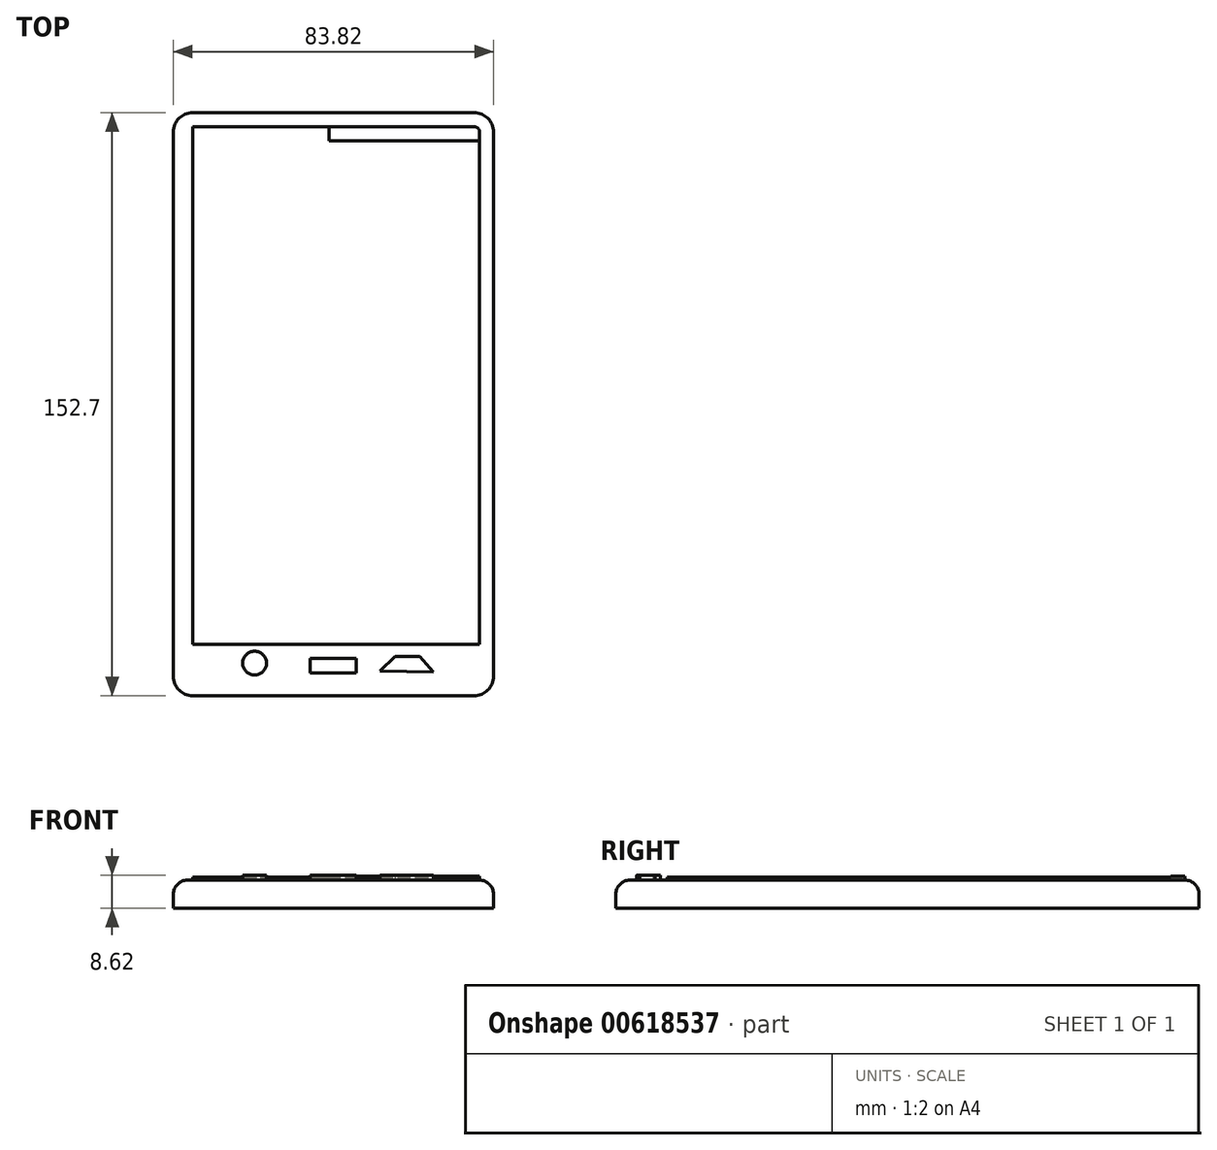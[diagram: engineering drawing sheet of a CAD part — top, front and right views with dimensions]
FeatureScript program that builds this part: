
annotation { "Feature Type Name" : "Feature", "Feature Type Description" : "" }
export const myFeature = defineFeature(function(context is Context, id is Id, definition is map)
    precondition{}
    {
        {
            var Q0;
            Q0=qCreatedBy(makeId("Top.planeOp"),FACE);
            var sketch = newSketch(context, id + "F0", { "sketchPlane" : qUnion([Q0])});
            skLineSegment(sketch, "E0.bottom", {"start": v(-77.85, 109.1) * mm, "end": v(5.97, 109.1) * mm});
            skLineSegment(sketch, "E0.top", {"start": v(-77.85, -43.6) * mm, "end": v(5.97, -43.6) * mm});
            skLineSegment(sketch, "E0.left", {"start": v(-77.85, 109.1) * mm, "end": v(-77.85, -43.6) * mm});
            skLineSegment(sketch, "E0.right", {"start": v(5.97, 109.1) * mm, "end": v(5.97, -43.6) * mm});
            skSolve(sketch);
        }
        {
            var Q0;
            Q0=makeQuery(id+"F0.imprint","IMPRINT",FACE,{"disambiguationData":[TD([[makeQuery(id+"F0.imprint","IMPRINT",EDGE,{"derivedFrom":sQuery(id+"F0.wireOp",EDGE,"E0.bottom")}),-1.0]])]});
            extrude(context, id + "F1", {"entities" : qUnion([Q0]), "depth" : 7.35 * mm, "offsetDistance" : 25.4 * mm});
        }
        {
            var Q0;
            Q0=makeQuery(id+"F1.opExtrude","SWEPT_EDGE",EDGE,{"disambiguationData":[OSD([sQuery(id+"F0.wireOp",EDGE,"E0.top"),sQuery(id+"F0.wireOp",EDGE,"E0.right")])]});
            var Q1;
            Q1=makeQuery(id+"F1.opExtrude","SWEPT_EDGE",EDGE,{"disambiguationData":[OSD([sQuery(id+"F0.wireOp",EDGE,"E0.top"),sQuery(id+"F0.wireOp",EDGE,"E0.left")])]});
            var Q2;
            Q2=makeQuery(id+"F1.opExtrude","SWEPT_EDGE",EDGE,{"disambiguationData":[OSD([sQuery(id+"F0.wireOp",EDGE,"E0.bottom"),sQuery(id+"F0.wireOp",EDGE,"E0.left")])]});
            var Q3;
            Q3=makeQuery(id+"F1.opExtrude","SWEPT_EDGE",EDGE,{"disambiguationData":[OSD([sQuery(id+"F0.wireOp",EDGE,"E0.bottom"),sQuery(id+"F0.wireOp",EDGE,"E0.right")])]});
            fillet(context, id + "F2", {"entities" : qUnion([Q0, Q1, Q2, Q3]), "radius" : 5.08 * mm, "tangentPropagation" : true, "allowEdgeOverflow" : false});
        }
        {
            var Q0;
            Q0=makeQuery(id+"F1.opExtrude","CAP_EDGE",EDGE,{"disambiguationData":[OSD([sQuery(id+"F0.wireOp",EDGE,"E0.right")])],"isStart":false});
            var Q1;
            Q1=makeQuery(id+"F1.opExtrude","CAP_EDGE",EDGE,{"disambiguationData":[OSD([sQuery(id+"F0.wireOp",EDGE,"E0.left")])],"isStart":false});
            fillet(context, id + "F3", {"entities" : qUnion([Q0, Q1]), "radius" : 3.68 * mm, "tangentPropagation" : true, "allowEdgeOverflow" : false});
        }
        {
            var Q0;
            Q0=makeQuery(id+"F1.opExtrude","CAP_FACE",FACE,{"disambiguationData":[OSD([sQuery(id+"F0.wireOp",EDGE,"E0.bottom"),sQuery(id+"F0.wireOp",EDGE,"E0.top"),sQuery(id+"F0.wireOp",EDGE,"E0.left"),sQuery(id+"F0.wireOp",EDGE,"E0.right")])],"isStart":false});
            var sketch = newSketch(context, id + "F4", { "sketchPlane" : qUnion([Q0])});
            skLineSegment(sketch, "E1.bottom", {"start": v(-72.77, 105.41) * mm, "end": v(2.29, 105.41) * mm});
            skLineSegment(sketch, "E1.top", {"start": v(-72.77, -30.16) * mm, "end": v(2.29, -30.16) * mm});
            skLineSegment(sketch, "E1.left", {"start": v(-72.77, 105.41) * mm, "end": v(-72.77, -30.16) * mm});
            skLineSegment(sketch, "E1.right", {"start": v(2.29, 105.41) * mm, "end": v(2.29, -30.16) * mm});
            skLineSegment(sketch, "E2.bottom", {"start": v(-42.1, -33.78) * mm, "end": v(-30.03, -33.78) * mm});
            skLineSegment(sketch, "E2.top", {"start": v(-42.1, -37.65) * mm, "end": v(-30.03, -37.65) * mm});
            skLineSegment(sketch, "E2.left", {"start": v(-42.1, -33.78) * mm, "end": v(-42.1, -37.65) * mm});
            skLineSegment(sketch, "E2.right", {"start": v(-30.03, -33.78) * mm, "end": v(-30.03, -37.65) * mm});
            skLineSegment(sketch, "E3", {"start": v(-56.59, -30.16) * mm, "end": v(-56.59, -39.93) * mm});
            skLineSegment(sketch, "E4", {"start": v(-56.59, -39.93) * mm, "end": v(-56.59, -35.04) * mm});
            skLineSegment(sketch, "E5", {"start": v(-56.59, -35.04) * mm, "end": v(-85.32, -35.04) * mm});
            skCircle(sketch, "E6", {"center": v(-56.59, -35.04) * mm, "radius": 3.12 * mm});
            skLineSegment(sketch, "E7", {"start": v(-23.75, -37.16) * mm, "end": v(-19.88, -33.3) * mm});
            skLineSegment(sketch, "E8", {"start": v(-19.88, -33.3) * mm, "end": v(-13.36, -33.3) * mm});
            skLineSegment(sketch, "E9", {"start": v(-13.36, -33.3) * mm, "end": v(-9.75, -37.4) * mm});
            skLineSegment(sketch, "E10", {"start": v(-23.75, -37.16) * mm, "end": v(-9.75, -37.4) * mm});
            skSolve(sketch);
        }
        {
            var Q0;
            {var subQ7=sQuery(id+"F4.wireOp",EDGE,"E1.top");Q0=makeQuery(id+"F4.imprint","IMPRINT",FACE,{"disambiguationData":[TD([[makeQuery(id+"F4.imprint","IMPRINT",EDGE,{"derivedFrom":subQ7}),1.0]])]});}
            extrude(context, id + "F5", {"entities" : qUnion([Q0]), "operationType" : NewBodyOperationType.ADD, "depth" : 0.76 * mm, "offsetDistance" : 25.4 * mm});
        }
        {
            var Q0;
            Q0=makeQuery(id+"F4.imprint","IMPRINT",FACE,{"disambiguationData":[TD([[makeQuery(id+"F4.imprint","IMPRINT",EDGE,{"derivedFrom":sQuery(id+"F4.wireOp",EDGE,"E2.bottom")}),-1.0]])]});
            var Q1;
            {var subQ1=sQuery(id+"F4.wireOp",EDGE,"E3");var subQ3=sQuery(id+"F4.wireOp",EDGE,"E6");var subQ4=makeQuery(id+"F4.imprint","INTERSECT",VERTEX,{"derivedFrom":[subQ1,subQ3]});Q1=makeQuery(id+"F4.imprint","IMPRINT",FACE,{"disambiguationData":[TD([[makeQuery(id+"F4.imprint","IMPRINT",EDGE,{"disambiguationData":[TD([[subQ4,1.0]])],"derivedFrom":subQ3}),1.0]])]});}
            var Q2;
            {var subQ1=sQuery(id+"F4.wireOp",EDGE,"E3");var subQ3=sQuery(id+"F4.wireOp",EDGE,"E6");var subQ4=makeQuery(id+"F4.imprint","INTERSECT",VERTEX,{"derivedFrom":[subQ1,subQ3]});Q2=makeQuery(id+"F4.imprint","IMPRINT",FACE,{"disambiguationData":[TD([[makeQuery(id+"F4.imprint","IMPRINT",EDGE,{"disambiguationData":[TD([[subQ4,-1.0]])],"derivedFrom":subQ3}),1.0]])]});}
            var Q3;
            {var subQ1=sQuery(id+"F4.wireOp",EDGE,"E4");var subQ3=sQuery(id+"F4.wireOp",EDGE,"E6");var subQ4=makeQuery(id+"F4.imprint","INTERSECT",VERTEX,{"derivedFrom":[subQ1,subQ3]});Q3=makeQuery(id+"F4.imprint","IMPRINT",FACE,{"disambiguationData":[TD([[makeQuery(id+"F4.imprint","IMPRINT",EDGE,{"disambiguationData":[TD([[subQ4,1.0]])],"derivedFrom":subQ3}),1.0]])]});}
            var Q4;
            Q4=makeQuery(id+"F4.imprint","IMPRINT",FACE,{"disambiguationData":[TD([[makeQuery(id+"F4.imprint","IMPRINT",EDGE,{"derivedFrom":sQuery(id+"F4.wireOp",EDGE,"E7")}),-1.0]])]});
            extrude(context, id + "F6", {"entities" : qUnion([Q0, Q1, Q2, Q3, Q4]), "operationType" : NewBodyOperationType.ADD, "depth" : 1.27 * mm, "offsetDistance" : 25.4 * mm});
        }
        {
            var Q0;
            Q0=makeQuery(id+"F5.opExtrude","CAP_FACE",FACE,{"disambiguationData":[OSD([sQuery(id+"F0.wireOp",EDGE,"E0.bottom"),sQuery(id+"F0.wireOp",EDGE,"E0.top"),sQuery(id+"F0.wireOp",EDGE,"E0.left"),sQuery(id+"F0.wireOp",EDGE,"E0.right"),sQuery(id+"F4.wireOp",EDGE,"E1.bottom"),sQuery(id+"F4.wireOp",EDGE,"E1.top"),sQuery(id+"F4.wireOp",EDGE,"E1.left"),sQuery(id+"F4.wireOp",EDGE,"E1.right")])],"isStart":false});
            var sketch = newSketch(context, id + "F7", { "sketchPlane" : qUnion([Q0])});
            skLineSegment(sketch, "E11.bottom", {"start": v(-72.77, 105.41) * mm, "end": v(2.29, 105.41) * mm});
            skLineSegment(sketch, "E11.top", {"start": v(-72.77, 101.68) * mm, "end": v(2.29, 101.68) * mm});
            skLineSegment(sketch, "E11.left", {"start": v(-72.77, 105.41) * mm, "end": v(-72.77, 101.68) * mm});
            skLineSegment(sketch, "E11.right", {"start": v(2.29, 105.41) * mm, "end": v(2.29, 101.68) * mm});
            skLineSegment(sketch, "E12", {"start": v(-72.77, 103.55) * mm, "end": v(2.29, 103.55) * mm});
            skLineSegment(sketch, "E13", {"start": v(-37.1, 101.68) * mm, "end": v(-37.1, 105.41) * mm});
            skCircle(sketch, "E14", {"center": v(-37.1, 103.55) * mm, "radius": 1.33 * mm});
            skSolve(sketch);
        }
        {
            var Q0;
            {var subQ0=sQuery(id+"F7.wireOp",EDGE,"E14");var subQ1=sQuery(id+"F7.wireOp",EDGE,"E12");var subQ2=makeQuery(id+"F7.imprint","INTERSECT",VERTEX,{"disambiguationData":[OD(0.0)],"derivedFrom":[subQ1,subQ0]});Q0=makeQuery(id+"F7.imprint","IMPRINT",FACE,{"disambiguationData":[TD([[makeQuery(id+"F7.imprint","IMPRINT",EDGE,{"disambiguationData":[TD([[subQ2,-1.0]])],"derivedFrom":subQ1}),-1.0]])]});}
            var Q1;
            {var subQ0=sQuery(id+"F7.wireOp",EDGE,"E13");var subQ1=sQuery(id+"F7.wireOp",EDGE,"E12");var subQ2=makeQuery(id+"F7.imprint","INTERSECT",VERTEX,{"derivedFrom":[subQ1,subQ0]});Q1=makeQuery(id+"F7.imprint","IMPRINT",FACE,{"disambiguationData":[TD([[makeQuery(id+"F7.imprint","IMPRINT",EDGE,{"disambiguationData":[TD([[subQ2,-1.0]])],"derivedFrom":subQ1}),-1.0]])]});}
            var Q2;
            {var subQ0=sQuery(id+"F7.wireOp",EDGE,"E13");var subQ1=sQuery(id+"F7.wireOp",EDGE,"E12");var subQ2=makeQuery(id+"F7.imprint","INTERSECT",VERTEX,{"derivedFrom":[subQ1,subQ0]});Q2=makeQuery(id+"F7.imprint","IMPRINT",FACE,{"disambiguationData":[TD([[makeQuery(id+"F7.imprint","IMPRINT",EDGE,{"disambiguationData":[TD([[subQ2,-1.0]])],"derivedFrom":subQ1}),1.0]])]});}
            var Q3;
            {var subQ0=sQuery(id+"F7.wireOp",EDGE,"E14");var subQ1=sQuery(id+"F7.wireOp",EDGE,"E12");var subQ2=makeQuery(id+"F7.imprint","INTERSECT",VERTEX,{"disambiguationData":[OD(0.0)],"derivedFrom":[subQ1,subQ0]});Q3=makeQuery(id+"F7.imprint","IMPRINT",FACE,{"disambiguationData":[TD([[makeQuery(id+"F7.imprint","IMPRINT",EDGE,{"disambiguationData":[TD([[subQ2,-1.0]])],"derivedFrom":subQ1}),1.0]])]});}
            extrude(context, id + "F8", {"entities" : qUnion([Q0, Q1, Q2, Q3]), "operationType" : NewBodyOperationType.ADD, "depth" : 0.25 * mm, "offsetDistance" : 25.4 * mm});
        }
    });
